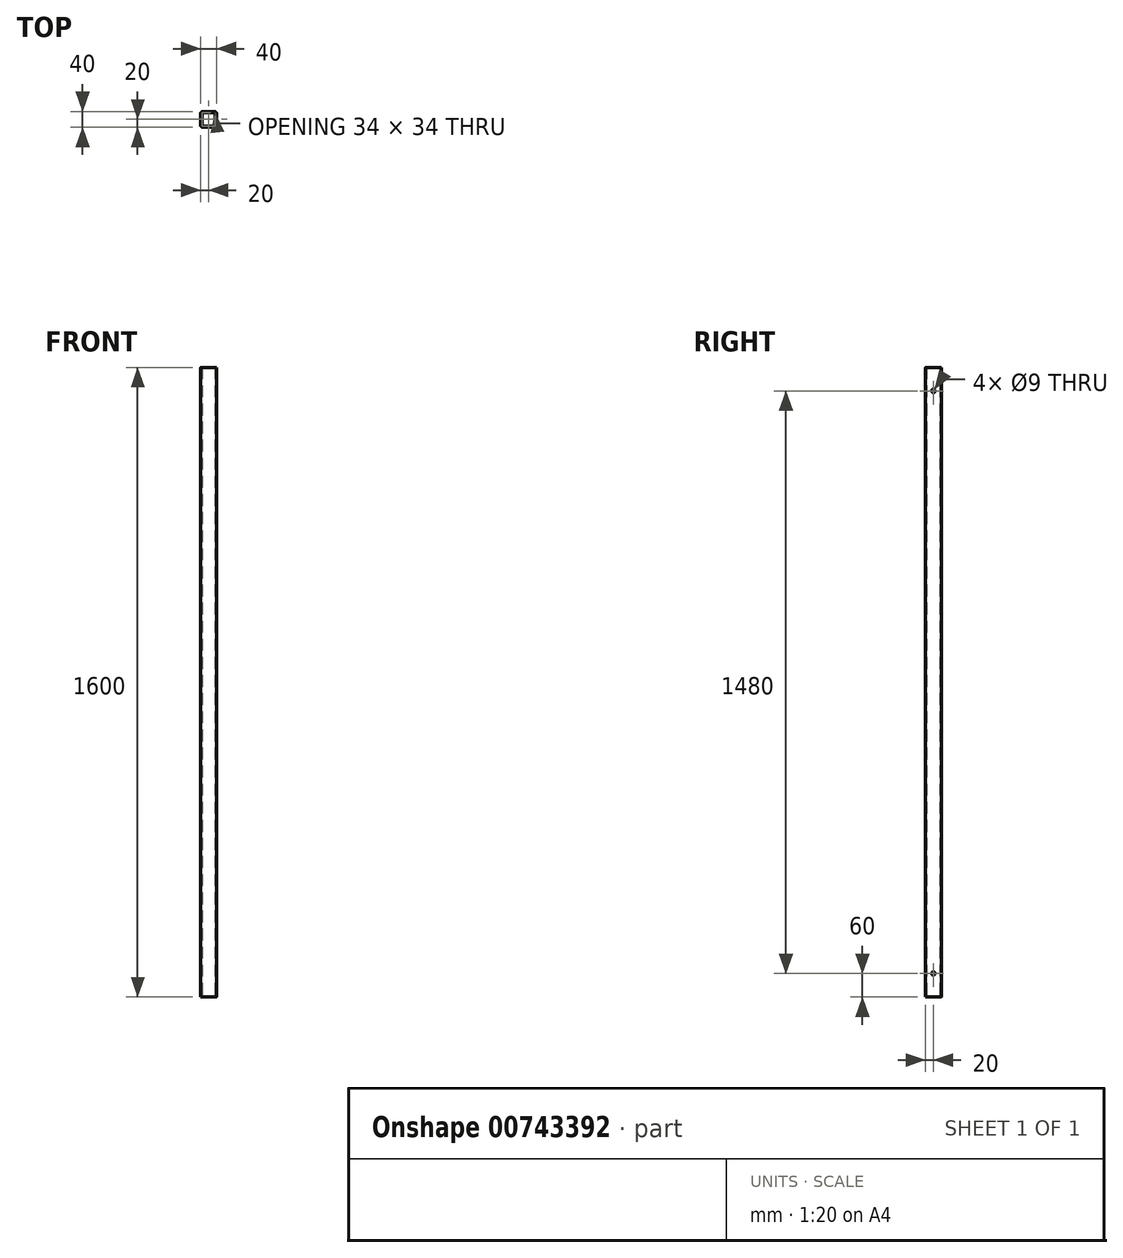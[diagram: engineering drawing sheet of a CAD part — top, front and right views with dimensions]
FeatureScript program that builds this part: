
annotation { "Feature Type Name" : "Feature", "Feature Type Description" : "" }
export const myFeature = defineFeature(function(context is Context, id is Id, definition is map)
    precondition{}
    {
        {
            var Q0;
            Q0=qCreatedBy(makeId("Top.planeOp"),FACE);
            var sketch = newSketch(context, id + "F0", { "sketchPlane" : qUnion([Q0])});
            skLineSegment(sketch, "E0.bottom", {"start": v(15.5, -20) * mm, "end": v(-15.5, -20) * mm});
            skLineSegment(sketch, "E0.top", {"start": v(15.5, 20) * mm, "end": v(-15.5, 20) * mm});
            skLineSegment(sketch, "E0.left", {"start": v(20, -15.5) * mm, "end": v(20, 15.5) * mm});
            skLineSegment(sketch, "E0.right", {"start": v(-20, -15.5) * mm, "end": v(-20, 15.5) * mm});
            skPoint(sketch, "E0.middle", {"position": v(0, 0) * mm});
            skPoint(sketch, "E1.visualSharp", {"position": v(-20, 20) * mm});
            skArc(sketch, "E2.filletArc", {"start": v(-15.5, 20) * mm, "mid": v(-18.68, 18.68) * mm, "end": v(-20, 15.5) * mm});
            skPoint(sketch, "E3.visualSharp", {"position": v(20, 20) * mm});
            skArc(sketch, "E3.filletArc", {"start": v(20, 15.5) * mm, "mid": v(18.68, 18.68) * mm, "end": v(15.5, 20) * mm});
            skPoint(sketch, "E4.visualSharp", {"position": v(20, -20) * mm});
            skArc(sketch, "E4.filletArc", {"start": v(15.5, -20) * mm, "mid": v(18.68, -18.68) * mm, "end": v(20, -15.5) * mm});
            skPoint(sketch, "E5.visualSharp", {"position": v(-20, -20) * mm});
            skArc(sketch, "E5.filletArc", {"start": v(-20, -15.5) * mm, "mid": v(-18.68, -18.68) * mm, "end": v(-15.5, -20) * mm});
            skArc(sketch, "E6.0", {"start": v(17, 15.5) * mm, "mid": v(16.56, 16.56) * mm, "end": v(15.5, 17) * mm});
            skLineSegment(sketch, "E6.1", {"start": v(17, -15.5) * mm, "end": v(17, 15.5) * mm});
            skLineSegment(sketch, "E6.2", {"start": v(15.5, 17) * mm, "end": v(-15.5, 17) * mm});
            skArc(sketch, "E6.3", {"start": v(15.5, -17) * mm, "mid": v(16.56, -16.56) * mm, "end": v(17, -15.5) * mm});
            skArc(sketch, "E6.4", {"start": v(-15.5, 17) * mm, "mid": v(-16.56, 16.56) * mm, "end": v(-17, 15.5) * mm});
            skLineSegment(sketch, "E6.5", {"start": v(-17, -15.5) * mm, "end": v(-17, 15.5) * mm});
            skArc(sketch, "E6.6", {"start": v(-17, -15.5) * mm, "mid": v(-16.56, -16.56) * mm, "end": v(-15.5, -17) * mm});
            skLineSegment(sketch, "E6.7", {"start": v(15.5, -17) * mm, "end": v(-15.5, -17) * mm});
            skSolve(sketch);
        }
        {
            var Q0;
            Q0=qSketchRegion(id+"F0",true);
            extrude(context, id + "F1", {"entities" : qUnion([Q0]), "depth" : 1600 * mm, "offsetDistance" : 25 * mm});
        }
        {
            var Q0;
            Q0=makeQuery(id+"F1.opExtrude","SWEPT_FACE",FACE,{"disambiguationData":[OSD([sQuery(id+"F0.wireOp",EDGE,"E0.left")])]});
            var sketch = newSketch(context, id + "F2", { "sketchPlane" : qUnion([Q0])});
            skLineSegment(sketch, "E7", {"start": v(0, 0) * mm, "end": v(0, 1600) * mm, "construction": true});
            skCircle(sketch, "E8", {"center": v(0, 1540) * mm, "radius": 4.5 * mm});
            skCircle(sketch, "E9", {"center": v(0, 60) * mm, "radius": 4.5 * mm});
            skSolve(sketch);
        }
        {
            var Q0;
            Q0 = qSketchRegion(id + "F2", true);
            extrude(context, id + "F3", {"entities" : qUnion([Q0]), "operationType" : NewBodyOperationType.REMOVE, "endBound" : BoundingType.THROUGH_ALL, "oppositeDirection" : true, "depth" : 25 * mm, "offsetDistance" : 25 * mm});
        }
    });
